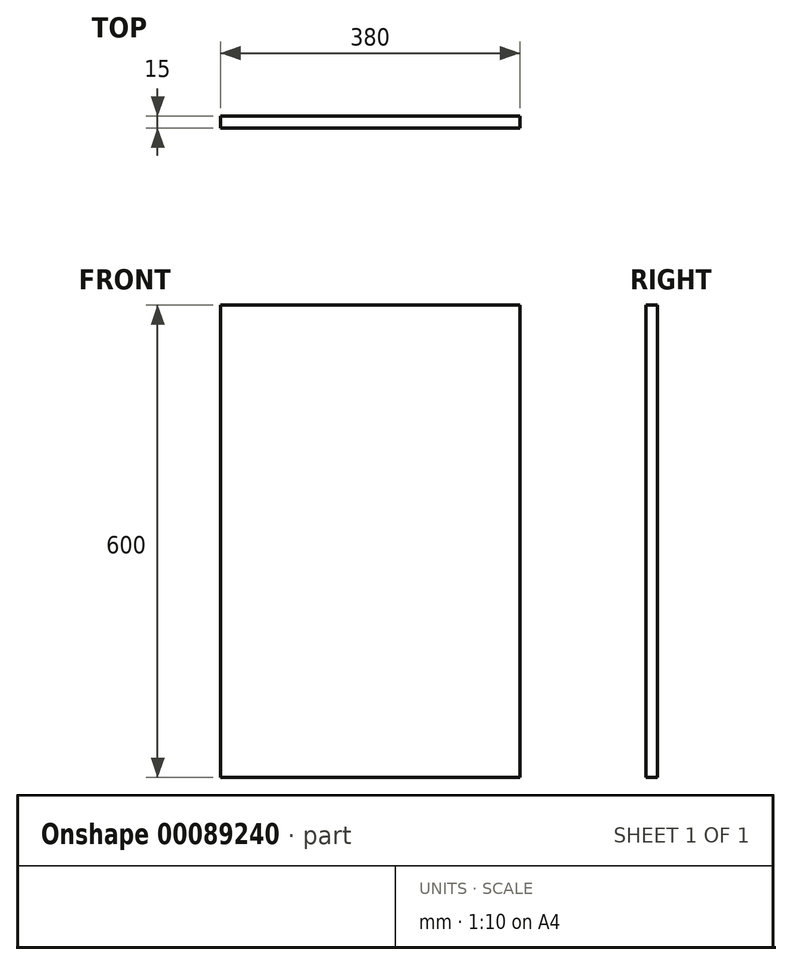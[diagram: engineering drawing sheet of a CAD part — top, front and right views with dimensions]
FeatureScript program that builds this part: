
annotation { "Feature Type Name" : "Feature", "Feature Type Description" : "" }
export const myFeature = defineFeature(function(context is Context, id is Id, definition is map)
    precondition{}
    {
        {
            var Q0;
            Q0=qCreatedBy(makeId("Front.planeOp"),FACE);
            var sketch = newSketch(context, id + "F0", { "sketchPlane" : qUnion([Q0])});
            skLineSegment(sketch, "E0.bottom", {"start": v(-190, 300) * mm, "end": v(190, 300) * mm});
            skLineSegment(sketch, "E0.top", {"start": v(-190, -300) * mm, "end": v(190, -300) * mm});
            skLineSegment(sketch, "E0.left", {"start": v(-190, 300) * mm, "end": v(-190, -300) * mm});
            skLineSegment(sketch, "E0.right", {"start": v(190, 300) * mm, "end": v(190, -300) * mm});
            skPoint(sketch, "E0.middle", {"position": v(0, 0) * mm});
            skSolve(sketch);
        }
        {
            var Q0;
            Q0=makeQuery(id+"F0.imprint","IMPRINT",FACE,{"disambiguationData":[TD([[makeQuery(id+"F0.imprint","IMPRINT",EDGE,{"derivedFrom":sQuery(id+"F0.wireOp",EDGE,"E0.bottom")}),-1.0]])]});
            extrude(context, id + "F1", {"entities" : qUnion([Q0]), "depth" : 15 * mm});
        }
    });
